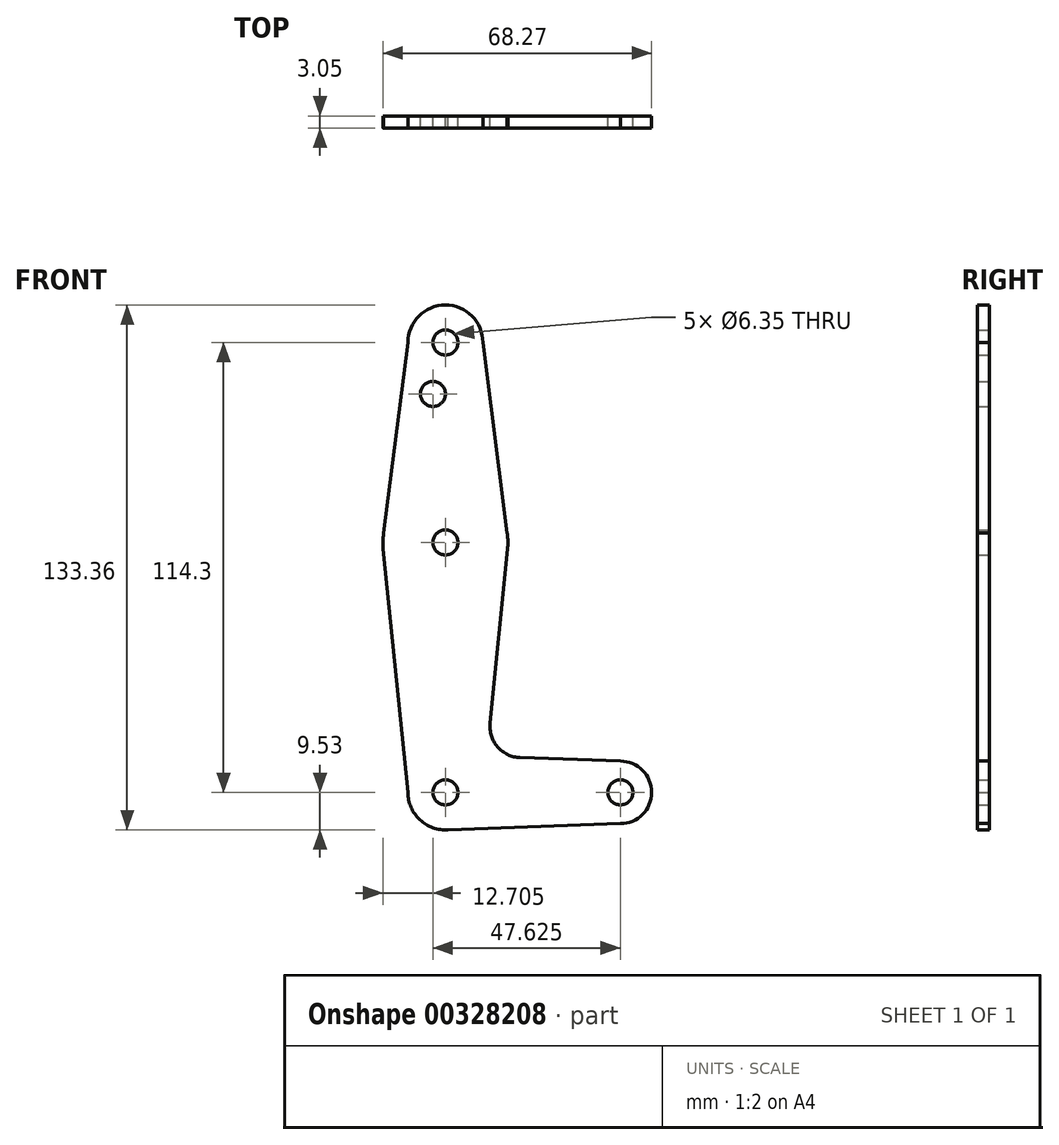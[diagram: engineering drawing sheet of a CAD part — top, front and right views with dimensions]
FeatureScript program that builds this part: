
annotation { "Feature Type Name" : "Feature", "Feature Type Description" : "" }
export const myFeature = defineFeature(function(context is Context, id is Id, definition is map)
    precondition{}
    {
        {
            var Q0;
            Q0=qCreatedBy(makeId("Front.planeOp"),FACE);
            var sketch = newSketch(context, id + "F0", { "sketchPlane" : qUnion([Q0])});
            skLineSegment(sketch, "E0", {"start": v(0, 0) * mm, "end": v(0, 114.3) * mm, "construction": true});
            skLineSegment(sketch, "E1", {"start": v(0, 0) * mm, "end": v(44.45, 0) * mm, "construction": true});
            skCircle(sketch, "E2", {"center": v(0, 0) * mm, "radius": 9.53 * mm});
            skCircle(sketch, "E3", {"center": v(0, 63.5) * mm, "radius": 15.88 * mm});
            skCircle(sketch, "E4", {"center": v(0, 114.3) * mm, "radius": 9.53 * mm});
            skCircle(sketch, "E5", {"center": v(44.45, 0) * mm, "radius": 7.94 * mm});
            skLineSegment(sketch, "E6", {"start": v(15.68, 65.96) * mm, "end": v(9.52, 114.3) * mm});
            skLineSegment(sketch, "E7", {"start": v(-15.68, 65.96) * mm, "end": v(-9.52, 114.3) * mm});
            skLineSegment(sketch, "E8", {"start": v(-15.8, 61.9) * mm, "end": v(-9.52, 0) * mm});
            skLineSegment(sketch, "E9", {"start": v(15.8, 61.9) * mm, "end": v(11.34, 17.59) * mm});
            skLineSegment(sketch, "E10", {"start": v(18.97, 8.85) * mm, "end": v(44.45, 7.94) * mm});
            skLineSegment(sketch, "E11", {"start": v(0, -9.52) * mm, "end": v(44.45, -7.94) * mm});
            skCircle(sketch, "E12", {"center": v(-3.18, 101.24) * mm, "radius": 3.18 * mm});
            skCircle(sketch, "E13", {"center": v(0, 63.5) * mm, "radius": 3.18 * mm});
            skCircle(sketch, "E14", {"center": v(0, 114.3) * mm, "radius": 3.18 * mm});
            skCircle(sketch, "E15", {"center": v(0, 0) * mm, "radius": 3.18 * mm});
            skCircle(sketch, "E16", {"center": v(44.45, 0) * mm, "radius": 3.18 * mm});
            skArc(sketch, "E17.filletArc", {"start": v(11.34, 17.59) * mm, "mid": v(13.26, 11.57) * mm, "end": v(18.97, 8.85) * mm});
            skSolve(sketch);
        }
        {
            var Q0;
            Q0 = qSketchRegion(id + "F0", true);
            extrude(context, id + "F1", {"entities" : qUnion([Q0]), "depth" : 3.05 * mm});
        }
    });
